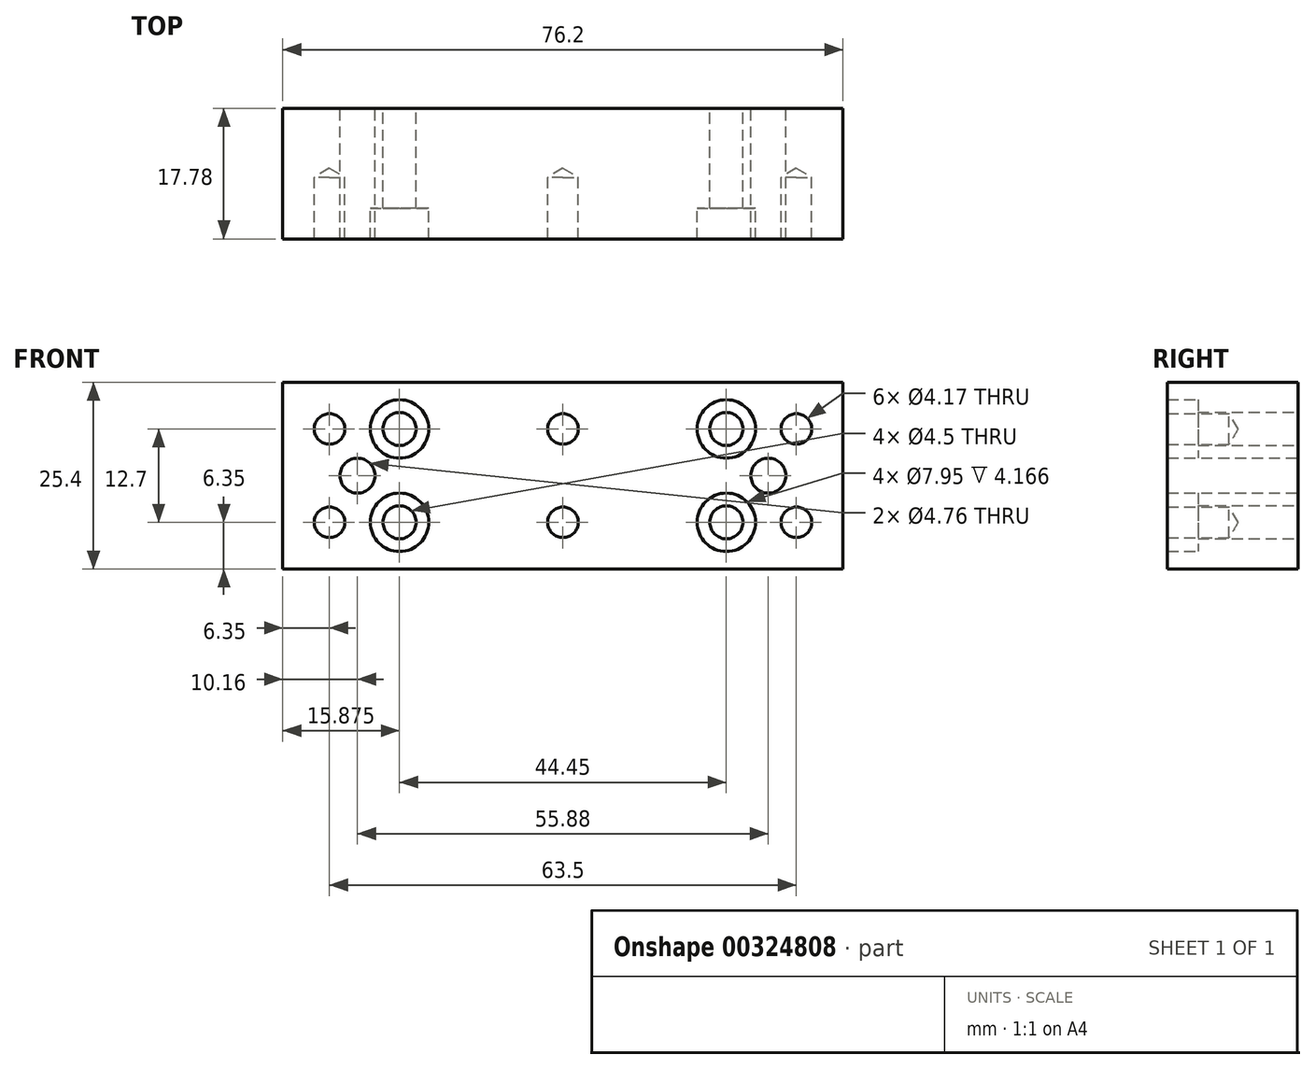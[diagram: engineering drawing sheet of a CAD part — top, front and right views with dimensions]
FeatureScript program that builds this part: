
annotation { "Feature Type Name" : "Feature", "Feature Type Description" : "" }
export const myFeature = defineFeature(function(context is Context, id is Id, definition is map)
    precondition{}
    {
        {
            var Q0;
            Q0=qCreatedBy(makeId("Front.planeOp"),FACE);
            var sketch = newSketch(context, id + "F0", { "sketchPlane" : qUnion([Q0])});
            skLineSegment(sketch, "E0.bottom", {"start": v(38.1, -12.7) * mm, "end": v(-38.1, -12.7) * mm});
            skLineSegment(sketch, "E0.top", {"start": v(38.1, 12.7) * mm, "end": v(-38.1, 12.7) * mm});
            skLineSegment(sketch, "E0.left", {"start": v(38.1, -12.7) * mm, "end": v(38.1, 12.7) * mm});
            skLineSegment(sketch, "E0.right", {"start": v(-38.1, -12.7) * mm, "end": v(-38.1, 12.7) * mm});
            skPoint(sketch, "E0.middle", {"position": v(0, 0) * mm});
            skSolve(sketch);
        }
        {
            var Q0;
            Q0=makeQuery(id+"F0.imprint","IMPRINT",FACE,{"disambiguationData":[TD([[makeQuery(id+"F0.imprint","IMPRINT",EDGE,{"derivedFrom":sQuery(id+"F0.wireOp",EDGE,"E0.bottom")}),-1.0]])]});
            extrude(context, id + "F1", {"entities" : qUnion([Q0]), "depth" : 17.78 * mm});
        }
        {
            var Q0;
            Q0=makeQuery(id+"F1.opExtrude","CAP_FACE",FACE,{"disambiguationData":[OSD([sQuery(id+"F0.wireOp",EDGE,"E0.bottom"),sQuery(id+"F0.wireOp",EDGE,"E0.top"),sQuery(id+"F0.wireOp",EDGE,"E0.left"),sQuery(id+"F0.wireOp",EDGE,"E0.right")])],"isStart":false});
            var sketch = newSketch(context, id + "F2", { "sketchPlane" : qUnion([Q0])});
            skPoint(sketch, "E1", {"position": v(-31.75, 6.35) * mm});
            skPoint(sketch, "E2", {"position": v(0, 6.35) * mm});
            skPoint(sketch, "E3", {"position": v(31.75, 6.35) * mm});
            skPoint(sketch, "E4", {"position": v(31.75, -6.35) * mm});
            skPoint(sketch, "E5", {"position": v(0, -6.35) * mm});
            skPoint(sketch, "E6", {"position": v(-31.75, -6.35) * mm});
            skSolve(sketch);
        }
        {
            var Q0;
            Q0=sQuery(id+"F2.wireOp",VERTEX,"E1");
            var Q1;
            Q1=sQuery(id+"F2.wireOp",VERTEX,"E2");
            var Q2;
            Q2=sQuery(id+"F2.wireOp",VERTEX,"E3");
            var Q3;
            Q3=sQuery(id+"F2.wireOp",VERTEX,"E4");
            var Q4;
            Q4=sQuery(id+"F2.wireOp",VERTEX,"E5");
            var Q5;
            Q5=sQuery(id+"F2.wireOp",VERTEX,"E6");
            var Q6;
            Q6=makeQuery(id+"F1.opExtrude","SWEPT_BODY",BODY,{"disambiguationData":[OSD([sQuery(id+"F0.wireOp",EDGE,"E0.bottom"),sQuery(id+"F0.wireOp",EDGE,"E0.top"),sQuery(id+"F0.wireOp",EDGE,"E0.left"),sQuery(id+"F0.wireOp",EDGE,"E0.right")])]});
            hole(context, id + "F3", {"style" : HoleStyle.SIMPLE, "endStyle" : HoleEndStyle.BLIND, "holeDiameter" : 4.17 * mm, "holeDepth" : 8.38 * mm, "tappedDepth" : 12.7 * mm, "tapClearance" : 3, "locations" : qUnion([Q0, Q1, Q2, Q3, Q4, Q5]), "scope" : qUnion([Q6])});
        }
        {
            var Q0;
            Q0=makeQuery(id+"F1.opExtrude","CAP_FACE",FACE,{"disambiguationData":[OSD([sQuery(id+"F0.wireOp",EDGE,"E0.bottom"),sQuery(id+"F0.wireOp",EDGE,"E0.top"),sQuery(id+"F0.wireOp",EDGE,"E0.left"),sQuery(id+"F0.wireOp",EDGE,"E0.right")])],"isStart":false});
            var sketch = newSketch(context, id + "F4", { "sketchPlane" : qUnion([Q0])});
            skPoint(sketch, "E7", {"position": v(-22.23, 6.35) * mm});
            skPoint(sketch, "E8", {"position": v(22.23, 6.35) * mm});
            skPoint(sketch, "E9", {"position": v(22.23, -6.35) * mm});
            skPoint(sketch, "E10", {"position": v(-22.23, -6.35) * mm});
            skSolve(sketch);
        }
        {
            var Q0;
            Q0=sQuery(id+"F4.wireOp",VERTEX,"E7");
            var Q1;
            Q1=sQuery(id+"F4.wireOp",VERTEX,"E8");
            var Q2;
            Q2=sQuery(id+"F4.wireOp",VERTEX,"E9");
            var Q3;
            Q3=sQuery(id+"F4.wireOp",VERTEX,"E10");
            var Q4;
            Q4=makeQuery(id+"F1.opExtrude","SWEPT_BODY",BODY,{"disambiguationData":[OSD([sQuery(id+"F0.wireOp",EDGE,"E0.bottom"),sQuery(id+"F0.wireOp",EDGE,"E0.top"),sQuery(id+"F0.wireOp",EDGE,"E0.left"),sQuery(id+"F0.wireOp",EDGE,"E0.right")])]});
            hole(context, id + "F5", {"style" : HoleStyle.C_BORE, "endStyle" : HoleEndStyle.THROUGH, "holeDiameter" : 4.5 * mm, "cBoreDiameter" : 7.95 * mm, "cBoreDepth" : 4.17 * mm, "tappedDepth" : 12.7 * mm, "tapClearance" : 3, "locations" : qUnion([Q0, Q1, Q2, Q3]), "scope" : qUnion([Q4])});
        }
        {
            var Q0;
            Q0=makeQuery(id+"F1.opExtrude","CAP_FACE",FACE,{"disambiguationData":[OSD([sQuery(id+"F0.wireOp",EDGE,"E0.bottom"),sQuery(id+"F0.wireOp",EDGE,"E0.top"),sQuery(id+"F0.wireOp",EDGE,"E0.left"),sQuery(id+"F0.wireOp",EDGE,"E0.right")])],"isStart":false});
            var sketch = newSketch(context, id + "F6", { "sketchPlane" : qUnion([Q0])});
            skPoint(sketch, "E11", {"position": v(-27.94, 0) * mm});
            skPoint(sketch, "E12", {"position": v(27.94, 0) * mm});
            skSolve(sketch);
        }
        {
            var Q0;
            Q0=sQuery(id+"F6.wireOp",VERTEX,"E11");
            var Q1;
            Q1=sQuery(id+"F6.wireOp",VERTEX,"E12");
            var Q2;
            Q2=makeQuery(id+"F1.opExtrude","SWEPT_BODY",BODY,{"disambiguationData":[OSD([sQuery(id+"F0.wireOp",EDGE,"E0.bottom"),sQuery(id+"F0.wireOp",EDGE,"E0.top"),sQuery(id+"F0.wireOp",EDGE,"E0.left"),sQuery(id+"F0.wireOp",EDGE,"E0.right")])]});
            hole(context, id + "F7", {"style" : HoleStyle.SIMPLE, "endStyle" : HoleEndStyle.THROUGH, "holeDiameter" : 4.76 * mm, "tappedDepth" : 12.7 * mm, "tapClearance" : 3, "locations" : qUnion([Q0, Q1]), "scope" : qUnion([Q2])});
        }
    });
